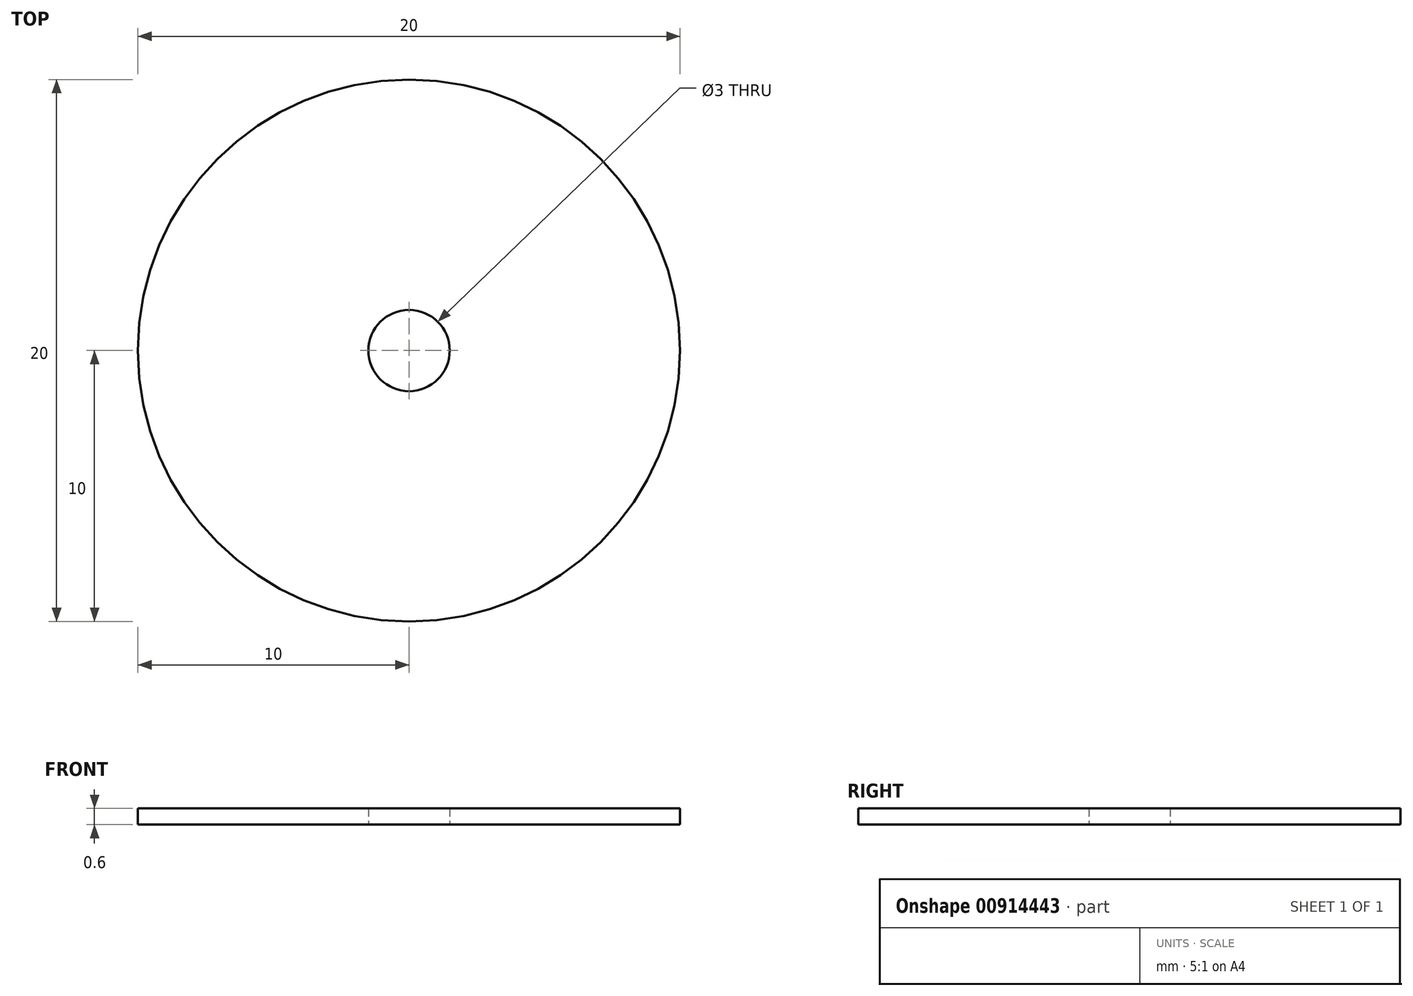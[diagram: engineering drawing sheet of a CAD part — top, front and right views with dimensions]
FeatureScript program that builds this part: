
annotation { "Feature Type Name" : "Feature", "Feature Type Description" : "" }
export const myFeature = defineFeature(function(context is Context, id is Id, definition is map)
    precondition{}
    {
        {
            var Q0;
            Q0=qCreatedBy(makeId("Top.planeOp"),FACE);
            var sketch = newSketch(context, id + "F0", { "sketchPlane" : qUnion([Q0])});
            skCircle(sketch, "E0", {"center": v(0, 0) * mm, "radius": 10 * mm});
            skCircle(sketch, "E1", {"center": v(0, 0) * mm, "radius": 1.5 * mm});
            skSolve(sketch);
        }
        {
            var Q0;
            Q0=makeQuery(id+"F0.imprint","IMPRINT",FACE,{"disambiguationData":[TD([[makeQuery(id+"F0.imprint","IMPRINT",EDGE,{"derivedFrom":sQuery(id+"F0.wireOp",EDGE,"E0")}),1.0]])]});
            extrude(context, id + "F1", {"entities" : qUnion([Q0]), "depth" : 0.6 * mm, "offsetDistance" : 25 * mm});
        }
    });
